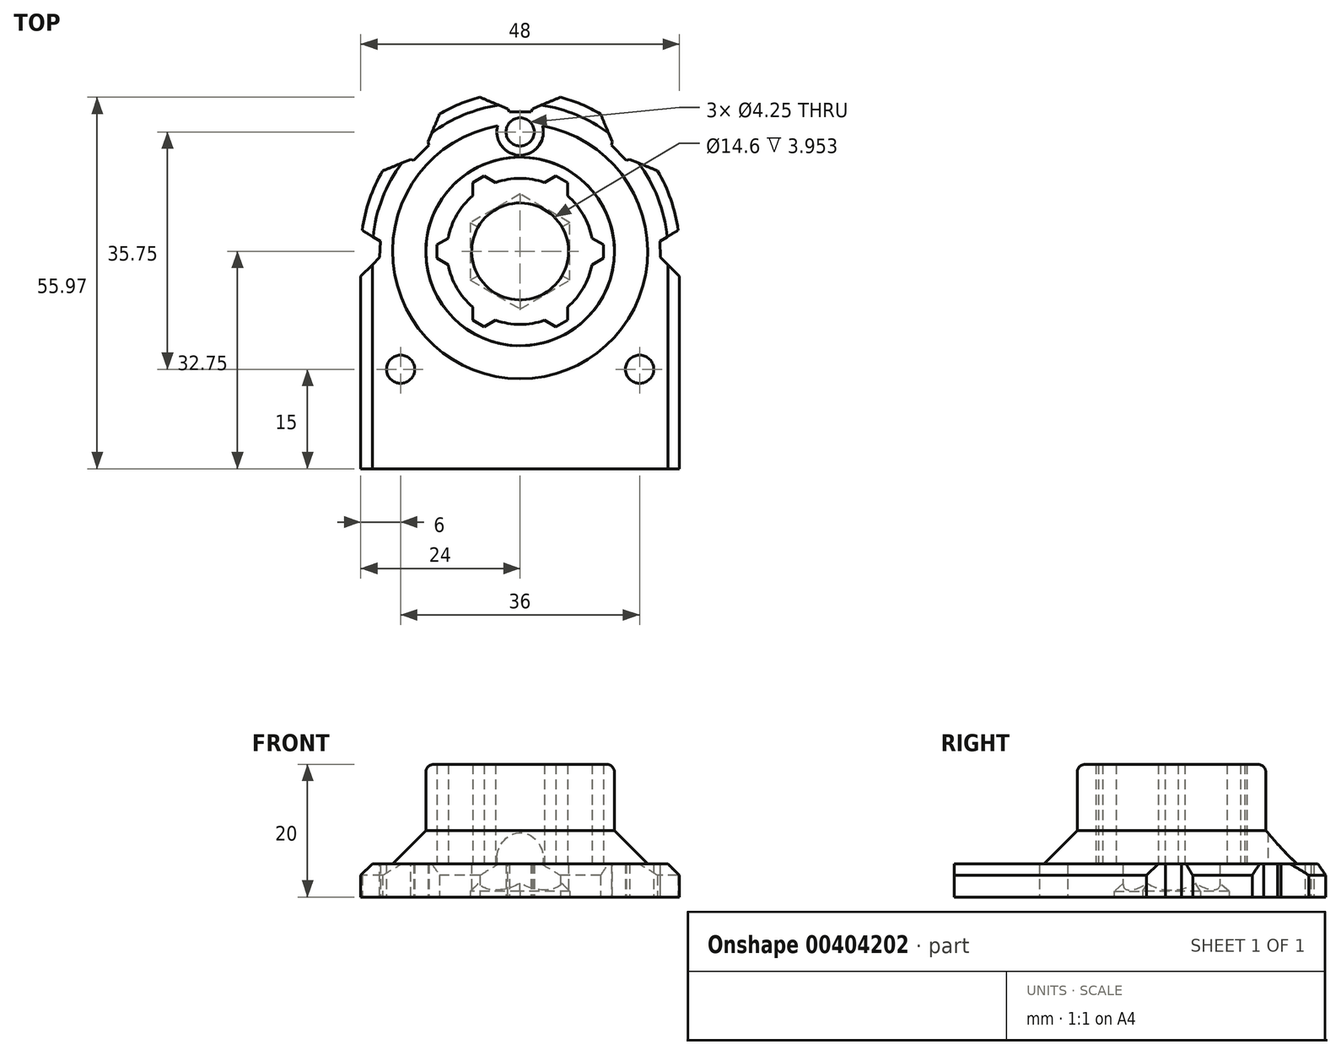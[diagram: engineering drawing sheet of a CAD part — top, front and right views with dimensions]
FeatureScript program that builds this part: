
annotation { "Feature Type Name" : "Feature", "Feature Type Description" : "" }
export const myFeature = defineFeature(function(context is Context, id is Id, definition is map)
    precondition{}
    {
        {
            var Q0;
            Q0=qCreatedBy(makeId("Top.planeOp"),FACE);
            var sketch = newSketch(context, id + "F0", { "sketchPlane" : qUnion([Q0])});
            skCircle(sketch, "E0", {"center": v(0, 0) * mm, "radius": 7.3 * mm});
            skArc(sketch, "E1", {"start": v(24, 0) * mm, "mid": v(22.74, 7.68) * mm, "end": v(19.08, 14.56) * mm});
            skLineSegment(sketch, "E2", {"start": v(-24, 0) * mm, "end": v(-24, -32.75) * mm});
            skLineSegment(sketch, "E3", {"start": v(-19, -32.75) * mm, "end": v(0, -32.75) * mm});
            skLineSegment(sketch, "E4", {"start": v(0, -32.75) * mm, "end": v(19, -32.75) * mm});
            skLineSegment(sketch, "E5", {"start": v(24, -32.75) * mm, "end": v(24, 0) * mm});
            skCircle(sketch, "E6", {"center": v(-18, -17.75) * mm, "radius": 2.12 * mm});
            skCircle(sketch, "E7.MirrorC", {"center": v(18, -17.75) * mm, "radius": 2.12 * mm});
            skCircle(sketch, "E8", {"center": v(0, 18) * mm, "radius": 2.12 * mm});
            skArc(sketch, "E9", {"start": v(-19, 0) * mm, "mid": v(0, 19) * mm, "end": v(19, 0) * mm, "construction": true});
            skLineSegment(sketch, "E10", {"start": v(-19, 0) * mm, "end": v(-19, -32.75) * mm, "construction": true});
            skLineSegment(sketch, "E11.MirrorCS", {"start": v(19, 0) * mm, "end": v(19, -32.75) * mm, "construction": true});
            skLineSegment(sketch, "E12", {"start": v(-24, -32.75) * mm, "end": v(-19, -32.75) * mm});
            skLineSegment(sketch, "E13", {"start": v(19, -32.75) * mm, "end": v(24, -32.75) * mm});
            skCircle(sketch, "E14.cCircle", {"center": v(0, 23.79) * mm, "radius": 2.77 * mm, "construction": true});
            skLineSegment(sketch, "E14.0", {"start": v(-1.6, 26.56) * mm, "end": v(1.6, 26.56) * mm, "construction": true});
            skLineSegment(sketch, "E14.1", {"start": v(1.6, 26.56) * mm, "end": v(3.2, 23.79) * mm, "construction": true});
            skLineSegment(sketch, "E14.2", {"start": v(3.2, 23.79) * mm, "end": v(1.6, 21.01) * mm});
            skLineSegment(sketch, "E14.3", {"start": v(1.6, 21.01) * mm, "end": v(-1.6, 21.01) * mm});
            skLineSegment(sketch, "E14.4", {"start": v(-1.6, 21.01) * mm, "end": v(-3.2, 23.79) * mm});
            skLineSegment(sketch, "E14.5", {"start": v(-3.2, 23.79) * mm, "end": v(-1.6, 26.56) * mm, "construction": true});
            skPoint(sketch, "E14.0.midPoint", {"position": v(0, 26.56) * mm});
            skArc(sketch, "E15.trimOffspring", {"start": v(-3.2, 23.79) * mm, "mid": v(-9.18, 22.17) * mm, "end": v(-14.56, 19.08) * mm});
            skLineSegment(sketch, "E16", {"start": v(0, 0) * mm, "end": v(-13.44, 13.44) * mm, "construction": true});
            skCircle(sketch, "E17.cCircle", {"center": v(-16.82, 16.82) * mm, "radius": 2.77 * mm, "construction": true});
            skLineSegment(sketch, "E17.0", {"start": v(-19.9, 17.65) * mm, "end": v(-17.65, 19.9) * mm, "construction": true});
            skLineSegment(sketch, "E17.1", {"start": v(-17.65, 19.9) * mm, "end": v(-14.56, 19.08) * mm, "construction": true});
            skLineSegment(sketch, "E17.2", {"start": v(-14.56, 19.08) * mm, "end": v(-13.73, 16) * mm});
            skLineSegment(sketch, "E17.3", {"start": v(-13.73, 16) * mm, "end": v(-16, 13.73) * mm});
            skLineSegment(sketch, "E17.4", {"start": v(-16, 13.73) * mm, "end": v(-19.08, 14.56) * mm});
            skLineSegment(sketch, "E17.5", {"start": v(-19.08, 14.56) * mm, "end": v(-19.9, 17.65) * mm, "construction": true});
            skPoint(sketch, "E17.0.midPoint", {"position": v(-18.78, 18.78) * mm});
            skLineSegment(sketch, "E18", {"start": v(-16.82, 16.82) * mm, "end": v(-13.44, 13.44) * mm, "construction": true});
            skLineSegment(sketch, "E19.MirrorCS", {"start": v(14.56, 19.08) * mm, "end": v(13.73, 16) * mm});
            skLineSegment(sketch, "E20.MirrorCS", {"start": v(13.73, 16) * mm, "end": v(16, 13.73) * mm});
            skLineSegment(sketch, "E21.MirrorCS", {"start": v(16, 13.73) * mm, "end": v(19.08, 14.56) * mm});
            skArc(sketch, "E22.trimOffspring", {"start": v(-19.08, 14.56) * mm, "mid": v(-22.74, 7.68) * mm, "end": v(-24, 0) * mm});
            skArc(sketch, "E23.trimOffspring", {"start": v(14.56, 19.08) * mm, "mid": v(9.18, 22.17) * mm, "end": v(3.2, 23.79) * mm});
            skSolve(sketch);
        }
        {
            var Q0;
            Q0=qSketchRegion(id+"F0",true);
            extrude(context, id + "F1", {"entities" : qUnion([Q0]), "depth" : 5 * mm});
        }
        {
            var Q0;
            Q0=makeQuery(id+"F1.opExtrude","CAP_FACE",FACE,{"disambiguationData":[OSD([sQuery(id+"F0.wireOp",EDGE,"E0"),sQuery(id+"F0.wireOp",EDGE,"E1"),sQuery(id+"F0.wireOp",EDGE,"E2"),sQuery(id+"F0.wireOp",EDGE,"E3"),sQuery(id+"F0.wireOp",EDGE,"E4"),sQuery(id+"F0.wireOp",EDGE,"E5"),sQuery(id+"F0.wireOp",EDGE,"E6"),sQuery(id+"F0.wireOp",EDGE,"E7.MirrorC"),sQuery(id+"F0.wireOp",EDGE,"E8")])],"isStart":false});
            var sketch = newSketch(context, id + "F2", { "sketchPlane" : qUnion([Q0])});
            skArc(sketch, "E24", {"start": v(10.82, 2) * mm, "mid": v(9.53, 5.5) * mm, "end": v(7.14, 8.37) * mm});
            skCircle(sketch, "E25.cCircle", {"center": v(10.82, 0) * mm, "radius": 1.73 * mm, "construction": true});
            skLineSegment(sketch, "E25.0", {"start": v(12.55, 1) * mm, "end": v(12.55, -1) * mm});
            skLineSegment(sketch, "E25.1", {"start": v(12.55, -1) * mm, "end": v(10.82, -2) * mm});
            skLineSegment(sketch, "E25.2", {"start": v(10.82, -2) * mm, "end": v(9.08, -1) * mm, "construction": true});
            skLineSegment(sketch, "E25.3", {"start": v(9.08, -1) * mm, "end": v(9.08, 1) * mm, "construction": true});
            skLineSegment(sketch, "E25.4", {"start": v(9.08, 1) * mm, "end": v(10.82, 2) * mm, "construction": true});
            skLineSegment(sketch, "E25.5", {"start": v(10.82, 2) * mm, "end": v(12.55, 1) * mm});
            skPoint(sketch, "E25.0.midPoint", {"position": v(12.55, 0) * mm});
            skLineSegment(sketch, "E26.1.0", {"start": v(3.68, 10.37) * mm, "end": v(5.4, 11.37) * mm});
            skLineSegment(sketch, "E26.1.1", {"start": v(5.4, 11.37) * mm, "end": v(7.14, 10.37) * mm});
            skLineSegment(sketch, "E26.1.2", {"start": v(7.14, 10.37) * mm, "end": v(7.14, 8.37) * mm});
            skLineSegment(sketch, "E26.2.0", {"start": v(-7.14, 8.37) * mm, "end": v(-7.14, 10.37) * mm});
            skLineSegment(sketch, "E26.2.1", {"start": v(-7.14, 10.37) * mm, "end": v(-5.4, 11.37) * mm});
            skLineSegment(sketch, "E26.2.2", {"start": v(-5.4, 11.37) * mm, "end": v(-3.68, 10.37) * mm});
            skLineSegment(sketch, "E26.3.0", {"start": v(-10.82, -2) * mm, "end": v(-12.55, -1) * mm});
            skLineSegment(sketch, "E26.3.1", {"start": v(-12.55, -1) * mm, "end": v(-12.55, 1) * mm});
            skLineSegment(sketch, "E26.3.2", {"start": v(-12.55, 1) * mm, "end": v(-10.82, 2) * mm});
            skLineSegment(sketch, "E26.4.0", {"start": v(-3.68, -10.37) * mm, "end": v(-5.4, -11.37) * mm});
            skLineSegment(sketch, "E26.4.1", {"start": v(-5.4, -11.37) * mm, "end": v(-7.14, -10.37) * mm});
            skLineSegment(sketch, "E26.4.2", {"start": v(-7.14, -10.37) * mm, "end": v(-7.14, -8.37) * mm});
            skLineSegment(sketch, "E26.5.0", {"start": v(7.14, -8.37) * mm, "end": v(7.14, -10.37) * mm});
            skLineSegment(sketch, "E26.5.1", {"start": v(7.14, -10.37) * mm, "end": v(5.4, -11.37) * mm});
            skLineSegment(sketch, "E26.5.2", {"start": v(5.4, -11.37) * mm, "end": v(3.68, -10.37) * mm});
            skArc(sketch, "E27.trimOffspring", {"start": v(3.68, 10.37) * mm, "mid": v(0, 11) * mm, "end": v(-3.68, 10.37) * mm});
            skArc(sketch, "E28.trimOffspring", {"start": v(-7.14, 8.37) * mm, "mid": v(-9.53, 5.5) * mm, "end": v(-10.82, 2) * mm});
            skArc(sketch, "E29.trimOffspring", {"start": v(-10.82, -2) * mm, "mid": v(-9.53, -5.5) * mm, "end": v(-7.14, -8.37) * mm});
            skArc(sketch, "E30.trimOffspring", {"start": v(7.14, -8.37) * mm, "mid": v(9.53, -5.5) * mm, "end": v(10.82, -2) * mm});
            skArc(sketch, "E31.trimOffspring", {"start": v(-3.68, -10.37) * mm, "mid": v(0, -11) * mm, "end": v(3.68, -10.37) * mm});
            skCircle(sketch, "E32", {"center": v(0, 0) * mm, "radius": 14.2 * mm});
            skSolve(sketch);
        }
        {
            var Q0;
            Q0=qSketchRegion(id+"F2",true);
            extrude(context, id + "F3", {"entities" : qUnion([Q0]), "operationType" : NewBodyOperationType.ADD, "depth" : 15 * mm});
        }
        {
            var Q0;
            Q0=makeQuery(id+"F3.opExtrude","CAP_EDGE",EDGE,{"disambiguationData":[OSD([sQuery(id+"F2.wireOp",EDGE,"E32")])],"isStart":true});
            chamfer(context, id + "F4", {"entities" : qUnion([Q0]), "width" : 5 * mm, "tangentPropagation" : true});
        }
        {
            var Q0;
            Q0=makeQuery(id+"F3.opExtrude","CAP_EDGE",EDGE,{"disambiguationData":[OSD([sQuery(id+"F2.wireOp",EDGE,"E32")])],"isStart":false});
            fillet(context, id + "F5", {"entities" : qUnion([Q0]), "radius" : 1.2 * mm, "tangentPropagation" : true, "allowEdgeOverflow" : false});
        }
        {
            var Q0;
            Q0=makeQuery(id+"F1.opExtrude","CAP_FACE",FACE,{"disambiguationData":[OSD([sQuery(id+"F0.wireOp",EDGE,"E0"),sQuery(id+"F0.wireOp",EDGE,"E1"),sQuery(id+"F0.wireOp",EDGE,"E2"),sQuery(id+"F0.wireOp",EDGE,"E3"),sQuery(id+"F0.wireOp",EDGE,"E4"),sQuery(id+"F0.wireOp",EDGE,"E5"),sQuery(id+"F0.wireOp",EDGE,"E6"),sQuery(id+"F0.wireOp",EDGE,"E7.MirrorC"),sQuery(id+"F0.wireOp",EDGE,"E8")])],"isStart":false});
            var sketch = newSketch(context, id + "F6", { "sketchPlane" : qUnion([Q0])});
            skCircle(sketch, "E33", {"center": v(0, 18) * mm, "radius": 3.5 * mm});
            skSolve(sketch);
        }
        {
            var Q0;
            Q0=qSketchRegion(id+"F6",true);
            extrude(context, id + "F7", {"entities" : qUnion([Q0]), "operationType" : NewBodyOperationType.REMOVE, "depth" : 25 * mm});
        }
        {
            var Q0;
            Q0=makeQuery(id+"F1.opExtrude","CAP_EDGE",EDGE,{"disambiguationData":[OSD([sQuery(id+"F0.wireOp",EDGE,"E1")])],"isStart":false});
            chamfer(context, id + "F8", {"entities" : qUnion([Q0]), "width" : 1.75 * mm, "tangentPropagation" : true});
        }
        {
            var Q0;
            Q0=makeQuery(id+"F1.opExtrude","CAP_FACE",FACE,{"disambiguationData":[OSD([sQuery(id+"F0.wireOp",EDGE,"E0"),sQuery(id+"F0.wireOp",EDGE,"E3"),sQuery(id+"F0.wireOp",EDGE,"E4"),sQuery(id+"F0.wireOp",EDGE,"E6"),sQuery(id+"F0.wireOp",EDGE,"E7.MirrorC"),sQuery(id+"F0.wireOp",EDGE,"E8"),sQuery(id+"F0.wireOp",EDGE,"E9"),sQuery(id+"F0.wireOp",EDGE,"E10"),sQuery(id+"F0.wireOp",EDGE,"E11.MirrorCS")])],"isStart":true});
            var sketch = newSketch(context, id + "F9", { "sketchPlane" : qUnion([Q0])});
            skCircle(sketch, "E34.cCircle", {"center": v(0, 0) * mm, "radius": 7.5 * mm, "construction": true});
            skLineSegment(sketch, "E34.0", {"start": v(-7.5, -4.33) * mm, "end": v(-7.5, 4.33) * mm});
            skLineSegment(sketch, "E34.1", {"start": v(-7.5, 4.33) * mm, "end": v(0, 8.66) * mm});
            skLineSegment(sketch, "E34.2", {"start": v(0, 8.66) * mm, "end": v(7.5, 4.33) * mm});
            skLineSegment(sketch, "E34.3", {"start": v(7.5, 4.33) * mm, "end": v(7.5, -4.33) * mm});
            skLineSegment(sketch, "E34.4", {"start": v(7.5, -4.33) * mm, "end": v(0, -8.66) * mm});
            skLineSegment(sketch, "E34.5", {"start": v(0, -8.66) * mm, "end": v(-7.5, -4.33) * mm});
            skPoint(sketch, "E34.0.midPoint", {"position": v(-7.5, 0) * mm});
            skSolve(sketch);
        }
        {
            var Q0;
            Q0 = qSketchRegion(id + "F9", true);
            extrude(context, id + "F10", {"entities" : qUnion([Q0]), "operationType" : NewBodyOperationType.REMOVE, "oppositeDirection" : true, "depth" : 2 * mm});
        }
        {
            var Q0;
            Q0=makeQuery(id+"F10.boolean.opBoolean","COPY",EDGE,{"derivedFrom":makeQuery(id+"F10.opExtrude","CAP_EDGE",EDGE,{"disambiguationData":[OSD([sQuery(id+"F9.wireOp",EDGE,"E34.5")])],"isStart":false})});
            var Q1;
            Q1=makeQuery(id+"F10.boolean.opBoolean","COPY",EDGE,{"derivedFrom":makeQuery(id+"F10.opExtrude","CAP_EDGE",EDGE,{"disambiguationData":[OSD([sQuery(id+"F9.wireOp",EDGE,"E34.4")])],"isStart":false})});
            var Q2;
            Q2=makeQuery(id+"F10.boolean.opBoolean","COPY",EDGE,{"derivedFrom":makeQuery(id+"F10.opExtrude","CAP_EDGE",EDGE,{"disambiguationData":[OSD([sQuery(id+"F9.wireOp",EDGE,"E34.3")])],"isStart":false})});
            var Q3;
            Q3=makeQuery(id+"F10.boolean.opBoolean","COPY",EDGE,{"derivedFrom":makeQuery(id+"F10.opExtrude","CAP_EDGE",EDGE,{"disambiguationData":[OSD([sQuery(id+"F9.wireOp",EDGE,"E34.0")])],"isStart":false})});
            var Q4;
            Q4=makeQuery(id+"F10.boolean.opBoolean","COPY",EDGE,{"derivedFrom":makeQuery(id+"F10.opExtrude","CAP_EDGE",EDGE,{"disambiguationData":[OSD([sQuery(id+"F9.wireOp",EDGE,"E34.1")])],"isStart":false})});
            var Q5;
            Q5=makeQuery(id+"F10.boolean.opBoolean","COPY",EDGE,{"derivedFrom":makeQuery(id+"F10.opExtrude","CAP_EDGE",EDGE,{"disambiguationData":[OSD([sQuery(id+"F9.wireOp",EDGE,"E34.2")])],"isStart":false})});
            chamfer(context, id + "F11", {"entities" : qUnion([Q0, Q1, Q2, Q3, Q4, Q5]), "width" : 1.15 * mm, "tangentPropagation" : true});
        }
        {
            var Q0;
            Q0=qCreatedBy(makeId("Top.planeOp"),FACE);
            var sketch = newSketch(context, id + "F12", { "sketchPlane" : qUnion([Q0])});
            skLineSegment(sketch, "E35", {"start": v(-16.82, 16.82) * mm, "end": v(0, 0) * mm, "construction": true});
            skCircle(sketch, "E36.cCircle", {"center": v(-23.9, 0) * mm, "radius": 2.77 * mm, "construction": true});
            skLineSegment(sketch, "E36.0", {"start": v(-21.07, 1.5) * mm, "end": v(-21.12, 0) * mm});
            skLineSegment(sketch, "E36.1", {"start": v(-21.18, -1.7) * mm, "end": v(-24, -3.2) * mm, "construction": true});
            skLineSegment(sketch, "E36.2", {"start": v(-24, -3.2) * mm, "end": v(-26.72, -1.5) * mm, "construction": true});
            skLineSegment(sketch, "E36.3", {"start": v(-26.72, -1.5) * mm, "end": v(-26.6, 1.7) * mm, "construction": true});
            skLineSegment(sketch, "E36.4", {"start": v(-26.6, 1.7) * mm, "end": v(-23.79, 3.2) * mm, "construction": true});
            skLineSegment(sketch, "E36.5", {"start": v(-23.79, 3.2) * mm, "end": v(-21.07, 1.5) * mm});
            skPoint(sketch, "E36.0.midPoint", {"position": v(-21.12, -0.1) * mm});
            skArc(sketch, "E37", {"start": v(-23.79, 3.2) * mm, "mid": v(-23.95, 1.6) * mm, "end": v(-24, 0) * mm});
            skLineSegment(sketch, "E38", {"start": v(-24, 0) * mm, "end": v(-21.12, 0) * mm});
            skLineSegment(sketch, "E39.MirrorCS", {"start": v(21.07, 1.5) * mm, "end": v(21.12, 0) * mm});
            skLineSegment(sketch, "E40.MirrorCS", {"start": v(26.72, -1.5) * mm, "end": v(26.6, 1.7) * mm, "construction": true});
            skLineSegment(sketch, "E41.MirrorCS", {"start": v(21.18, -1.7) * mm, "end": v(24, -3.2) * mm, "construction": true});
            skLineSegment(sketch, "E42.MirrorCS", {"start": v(24, -3.2) * mm, "end": v(26.72, -1.5) * mm, "construction": true});
            skLineSegment(sketch, "E43.MirrorCS", {"start": v(23.79, 3.2) * mm, "end": v(21.07, 1.5) * mm});
            skLineSegment(sketch, "E44.MirrorCS", {"start": v(24, 0) * mm, "end": v(21.12, 0) * mm});
            skCircle(sketch, "E45.MirrorC", {"center": v(23.9, 0) * mm, "radius": 2.77 * mm, "construction": true});
            skLineSegment(sketch, "E46.MirrorCS", {"start": v(26.6, 1.7) * mm, "end": v(23.79, 3.2) * mm, "construction": true});
            skPoint(sketch, "E47.MirrorP", {"position": v(21.12, -0.1) * mm});
            skArc(sketch, "E48.MirrorCS", {"start": v(23.79, 3.2) * mm, "mid": v(23.95, 1.6) * mm, "end": v(24, 0) * mm});
            skSolve(sketch);
        }
        {
            var Q0;
            Q0 = qSketchRegion(id + "F12", true);
            extrude(context, id + "F13", {"entities" : qUnion([Q0]), "operationType" : NewBodyOperationType.REMOVE, "depth" : 25 * mm});
        }
        {
            var Q0;
            Q0=makeQuery(id+"F13.boolean.opBoolean","MERGE",EDGE,{"derivedFrom":[makeQuery(id+"F1.opExtrude","SWEPT_EDGE",EDGE,{"disambiguationData":[OSD([sQuery(id+"F0.wireOp",EDGE,"E2"),sQuery(id+"F0.wireOp",EDGE,"E22.trimOffspring")])]}),makeQuery(id+"F13.opExtrude","SWEPT_EDGE",EDGE,{"disambiguationData":[OSD([sQuery(id+"F12.wireOp",EDGE,"E37"),sQuery(id+"F12.wireOp",EDGE,"E38")])]})]});
            var Q1;
            Q1=makeQuery(id+"F13.boolean.opBoolean","COPY",EDGE,{"derivedFrom":makeQuery(id+"F13.opExtrude","SWEPT_EDGE",EDGE,{"disambiguationData":[OSD([sQuery(id+"F12.wireOp",EDGE,"E36.5"),sQuery(id+"F12.wireOp",EDGE,"E37")])]})});
            var Q2;
            Q2=makeQuery(id+"F1.opExtrude","SWEPT_EDGE",EDGE,{"disambiguationData":[OSD([sQuery(id+"F0.wireOp",EDGE,"E17.4"),sQuery(id+"F0.wireOp",EDGE,"E22.trimOffspring")])]});
            var Q3;
            Q3=makeQuery(id+"F1.opExtrude","SWEPT_EDGE",EDGE,{"disambiguationData":[OSD([sQuery(id+"F0.wireOp",EDGE,"E15.trimOffspring"),sQuery(id+"F0.wireOp",EDGE,"E17.2")])]});
            var Q4;
            Q4=makeQuery(id+"F1.opExtrude","SWEPT_EDGE",EDGE,{"disambiguationData":[OSD([sQuery(id+"F0.wireOp",EDGE,"E19.MirrorCS"),sQuery(id+"F0.wireOp",EDGE,"E23.trimOffspring")])]});
            var Q5;
            Q5=makeQuery(id+"F1.opExtrude","SWEPT_EDGE",EDGE,{"disambiguationData":[OSD([sQuery(id+"F0.wireOp",EDGE,"E1"),sQuery(id+"F0.wireOp",EDGE,"E21.MirrorCS")])]});
            var Q6;
            Q6=makeQuery(id+"F13.boolean.opBoolean","MERGE",EDGE,{"derivedFrom":[makeQuery(id+"F1.opExtrude","SWEPT_EDGE",EDGE,{"disambiguationData":[OSD([sQuery(id+"F0.wireOp",EDGE,"E1"),sQuery(id+"F0.wireOp",EDGE,"E5")])]}),makeQuery(id+"F13.opExtrude","SWEPT_EDGE",EDGE,{"disambiguationData":[OSD([sQuery(id+"F12.wireOp",EDGE,"E44.MirrorCS"),sQuery(id+"F12.wireOp",EDGE,"E48.MirrorCS")])]})]});
            var Q7;
            Q7=makeQuery(id+"F13.boolean.opBoolean","COPY",EDGE,{"derivedFrom":makeQuery(id+"F13.opExtrude","SWEPT_EDGE",EDGE,{"disambiguationData":[OSD([sQuery(id+"F12.wireOp",EDGE,"E43.MirrorCS"),sQuery(id+"F12.wireOp",EDGE,"E48.MirrorCS")])]})});
            var Q8;
            Q8=makeQuery(id+"F1.opExtrude","SWEPT_EDGE",EDGE,{"disambiguationData":[OSD([sQuery(id+"F0.wireOp",EDGE,"E14.2"),sQuery(id+"F0.wireOp",EDGE,"E23.trimOffspring")])]});
            var Q9;
            Q9=makeQuery(id+"F1.opExtrude","SWEPT_EDGE",EDGE,{"disambiguationData":[OSD([sQuery(id+"F0.wireOp",EDGE,"E14.4"),sQuery(id+"F0.wireOp",EDGE,"E15.trimOffspring")])]});
            chamfer(context, id + "F14", {"entities" : qUnion([Q0, Q1, Q2, Q3, Q4, Q5, Q6, Q7, Q8, Q9]), "width" : 3.75 * mm, "tangentPropagation" : true});
        }
        {
            var Q0;
            Q0=makeQuery(id+"F1.opExtrude","CAP_EDGE",EDGE,{"disambiguationData":[OSD([sQuery(id+"F0.wireOp",EDGE,"E2")])],"isStart":false});
            var Q1;
            Q1=makeQuery(id+"F1.opExtrude","CAP_EDGE",EDGE,{"disambiguationData":[OSD([sQuery(id+"F0.wireOp",EDGE,"E22.trimOffspring")])],"isStart":false});
            var Q2;
            Q2=makeQuery(id+"F1.opExtrude","CAP_EDGE",EDGE,{"disambiguationData":[OSD([sQuery(id+"F0.wireOp",EDGE,"E15.trimOffspring")])],"isStart":false});
            var Q3;
            Q3=makeQuery(id+"F1.opExtrude","CAP_EDGE",EDGE,{"disambiguationData":[OSD([sQuery(id+"F0.wireOp",EDGE,"E23.trimOffspring")])],"isStart":false});
            chamfer(context, id + "F15", {"entities" : qUnion([Q0, Q1, Q2, Q3]), "width" : 1.75 * mm, "tangentPropagation" : true});
        }
    });
